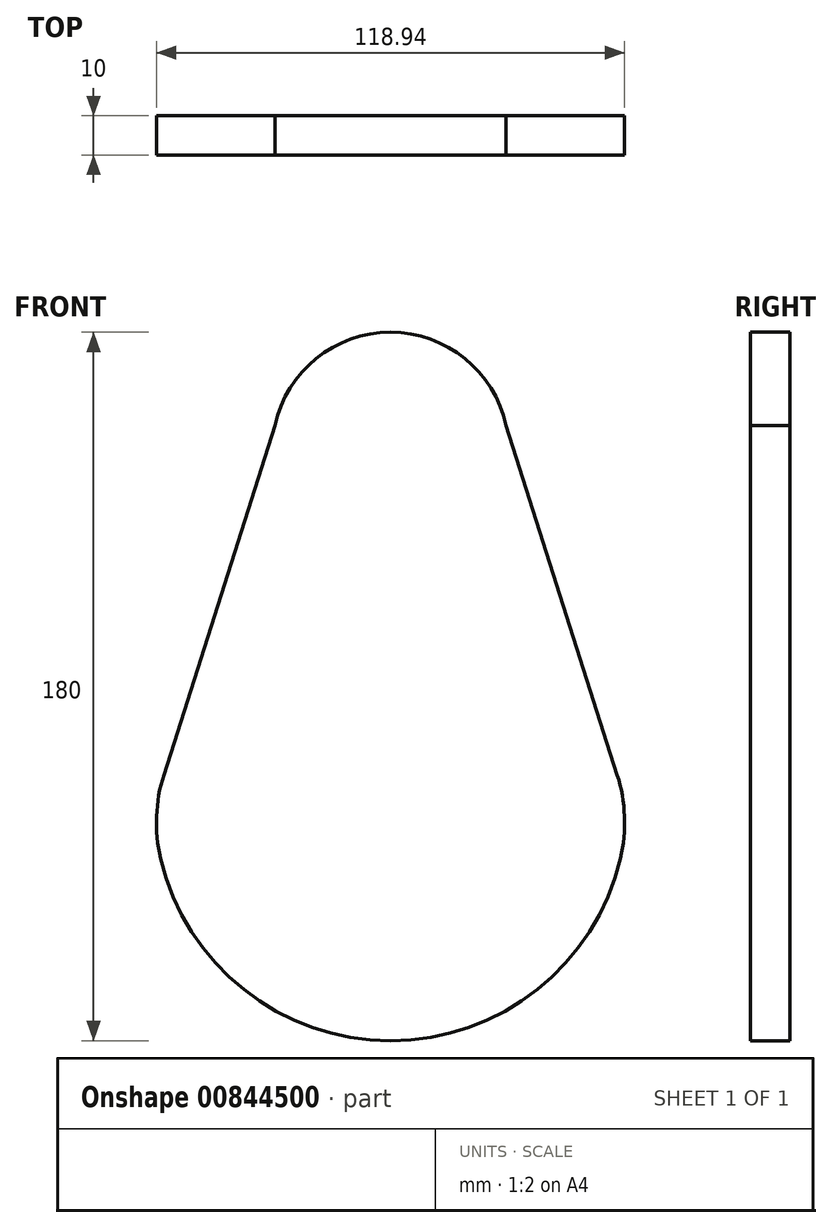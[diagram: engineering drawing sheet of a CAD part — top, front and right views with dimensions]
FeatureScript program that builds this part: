
annotation { "Feature Type Name" : "Feature", "Feature Type Description" : "" }
export const myFeature = defineFeature(function(context is Context, id is Id, definition is map)
    precondition{}
    {
        {
            var Q0;
            Q0=qCreatedBy(makeId("Front.planeOp"),FACE);
            var sketch = newSketch(context, id + "F0", { "sketchPlane" : qUnion([Q0])});
            skArc(sketch, "E0", {"start": v(-58.42, -13.68) * mm, "mid": v(0, -60) * mm, "end": v(58.42, -13.68) * mm});
            skLineSegment(sketch, "E1", {"start": v(0, 60) * mm, "end": v(0, 120) * mm});
            skArc(sketch, "E2", {"start": v(29.34, 96.26) * mm, "mid": v(0, 120) * mm, "end": v(-29.34, 96.26) * mm});
            skPoint(sketch, "E3.first.point", {"position": v(-255.14, 147.4) * mm});
            skPoint(sketch, "E3.second.point", {"position": v(-29.34, 96.26) * mm});
            skPoint(sketch, "E3.third.point", {"position": v(-60, 0) * mm});
            skLineSegment(sketch, "E4", {"start": v(-29.34, 96.26) * mm, "end": v(-57.59, 7.58) * mm});
            skLineSegment(sketch, "E5.MirrorCS", {"start": v(29.34, 96.26) * mm, "end": v(57.59, 7.58) * mm});
            skArc(sketch, "E6.filletArc", {"start": v(-57.59, 7.58) * mm, "mid": v(-59.44, -3) * mm, "end": v(-58.42, -13.68) * mm});
            skPoint(sketch, "E7.visualSharp", {"position": v(60, 0) * mm});
            skArc(sketch, "E7.filletArc", {"start": v(58.42, -13.68) * mm, "mid": v(59.44, -3) * mm, "end": v(57.59, 7.58) * mm});
            skSolve(sketch);
        }
        {
            var Q0;
            Q0=makeQuery(id+"F0.imprint","IMPRINT",FACE,{"disambiguationData":[TD([[makeQuery(id+"F0.imprint","IMPRINT",EDGE,{"derivedFrom":sQuery(id+"F0.wireOp",EDGE,"E0")}),1.0]])]});
            extrude(context, id + "F1", {"entities" : qUnion([Q0]), "depth" : 10 * mm, "offsetDistance" : 25 * mm});
        }
    });
